# Revit family: FU_Chair_Sandler_OSWELL TASK 1-1PP
name_source: partatom
category: Furniture
units: mm (PartAtom-declared; Revit-internal decimal feet)

## family parameters
Always vertical = Yes
Cut with Voids When Loaded = No
OmniClass Number = 23.40.20.00
OmniClass Title = General Furniture and Specialties
Render Appearance Source = Family Geometry
Room Calculation Point = No
Shared = No
Work Plane-Based = No

## types (1)
- Oswell Task 1.1PP
    Default Elevation = 0 mm  [stored 0 ft]
    Depth = 620 mm  [stored 2.03412 ft]
    Description = Swivel task chair with 5-spoke aluminum base on caster wheels. This height-adjustable chair is made of ridged polypropylene, featuring a non-slip texture. Greenguard Gold-certified.
    Height = 815 mm  [stored 2.67388 ft]
    Manufacturer = Sandler
    Model = Oswell Task 1.1PP
    URL = https://www.sandlerseating.com
    Width = 680 mm  [stored 2.23097 ft]

note: [stored X ft] marks values corroborated as IEEE doubles in the binary element streams (Revit-internal decimal feet)

## geometry (parser evidence)
native form markers: Sweep x14
no freeform markers — native parametric forms only
